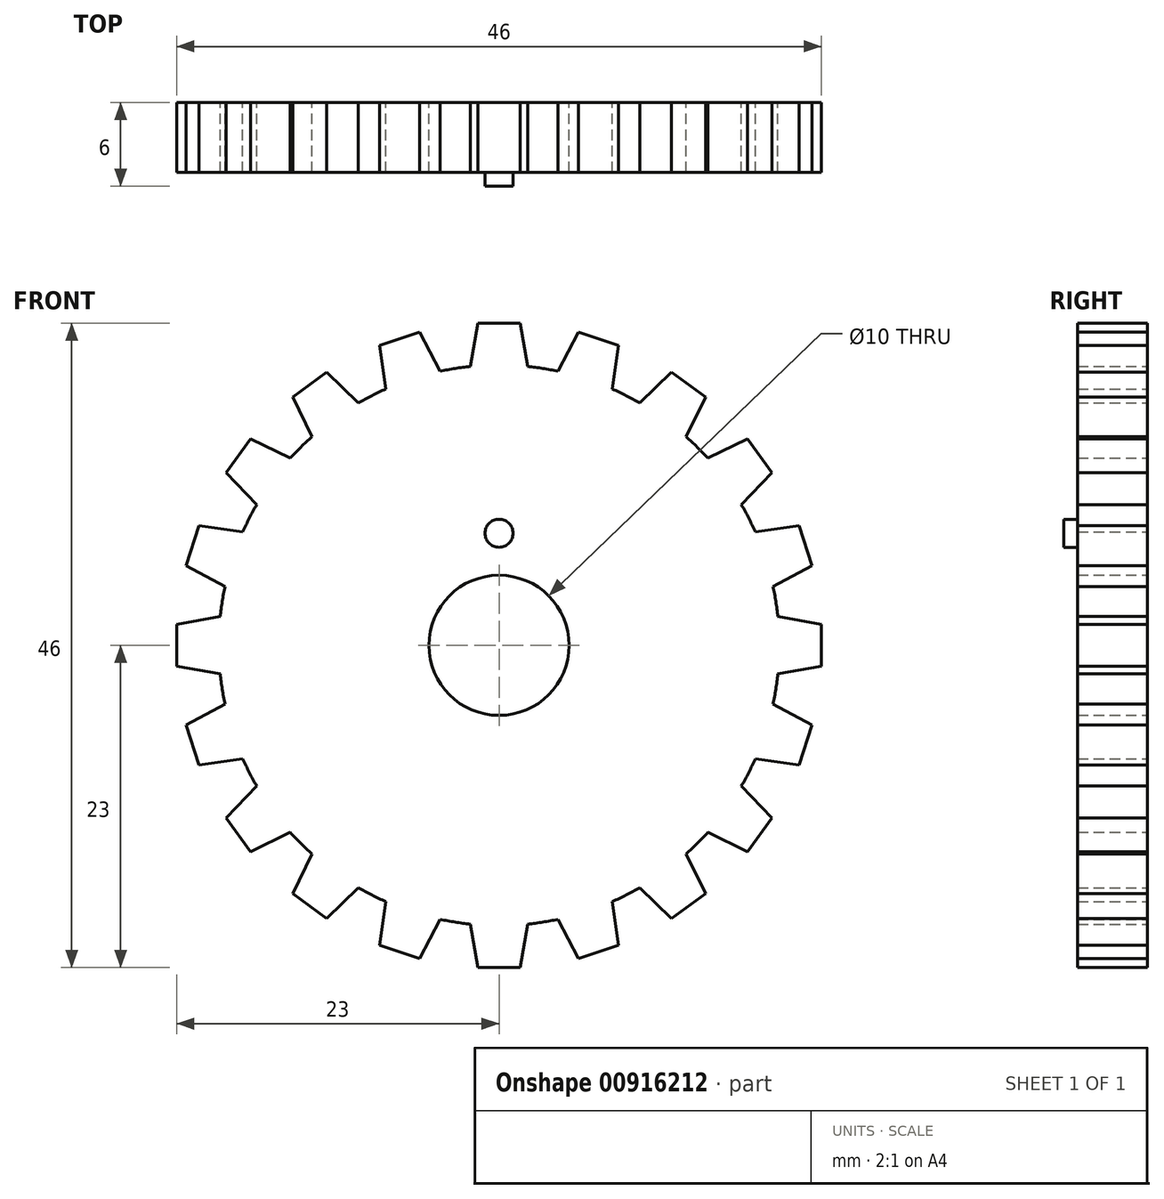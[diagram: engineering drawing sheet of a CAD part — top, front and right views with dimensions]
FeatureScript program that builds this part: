
annotation { "Feature Type Name" : "Feature", "Feature Type Description" : "" }
export const myFeature = defineFeature(function(context is Context, id is Id, definition is map)
    precondition{}
    {
        {
            var Q0;
            Q0=qCreatedBy(makeId("Front.planeOp"),FACE);
            var sketch = newSketch(context, id + "F0", { "sketchPlane" : qUnion([Q0])});
            skCircle(sketch, "E0", {"center": v(0, 0) * mm, "radius": 5 * mm});
            skCircle(sketch, "E1", {"center": v(0, 0) * mm, "radius": 20 * mm});
            skLineSegment(sketch, "E2", {"start": v(0, 23) * mm, "end": v(1.5, 23) * mm});
            skLineSegment(sketch, "E3", {"start": v(1.5, 23) * mm, "end": v(2.05, 19.9) * mm});
            skLineSegment(sketch, "E4.MirrorCS", {"start": v(0, 23) * mm, "end": v(-1.5, 23) * mm});
            skLineSegment(sketch, "E5.MirrorCS", {"start": v(-1.5, 23) * mm, "end": v(-2.05, 19.9) * mm});
            skLineSegment(sketch, "E6.1.0", {"start": v(-8.53, 21.41) * mm, "end": v(-8.1, 18.29) * mm});
            skLineSegment(sketch, "E6.1.1", {"start": v(-7.1, 21.87) * mm, "end": v(-8.53, 21.41) * mm});
            skLineSegment(sketch, "E6.1.2", {"start": v(-7.1, 21.87) * mm, "end": v(-5.68, 22.34) * mm});
            skLineSegment(sketch, "E6.1.3", {"start": v(-5.68, 22.34) * mm, "end": v(-4.2, 19.55) * mm});
            skLineSegment(sketch, "E6.2.0", {"start": v(-14.73, 17.73) * mm, "end": v(-13.35, 14.9) * mm});
            skLineSegment(sketch, "E6.2.1", {"start": v(-13.52, 18.6) * mm, "end": v(-14.73, 17.73) * mm});
            skLineSegment(sketch, "E6.2.2", {"start": v(-13.52, 18.6) * mm, "end": v(-12.3, 19.49) * mm});
            skLineSegment(sketch, "E6.2.3", {"start": v(-12.3, 19.49) * mm, "end": v(-10.04, 17.3) * mm});
            skLineSegment(sketch, "E7.2.3.0", {"start": v(-19.49, 12.3) * mm, "end": v(-17.3, 10.04) * mm});
            skLineSegment(sketch, "E7.3.3.0", {"start": v(-18.6, 13.52) * mm, "end": v(-19.49, 12.3) * mm});
            skLineSegment(sketch, "E7.6.3.0", {"start": v(-18.6, 13.52) * mm, "end": v(-17.73, 14.73) * mm});
            skLineSegment(sketch, "E7.9.3.0", {"start": v(-17.73, 14.73) * mm, "end": v(-14.9, 13.35) * mm});
            skLineSegment(sketch, "E7.2.4.0", {"start": v(-22.34, 5.68) * mm, "end": v(-19.55, 4.2) * mm});
            skLineSegment(sketch, "E7.3.4.0", {"start": v(-21.87, 7.1) * mm, "end": v(-22.34, 5.68) * mm});
            skLineSegment(sketch, "E7.6.4.0", {"start": v(-21.87, 7.1) * mm, "end": v(-21.41, 8.53) * mm});
            skLineSegment(sketch, "E7.9.4.0", {"start": v(-21.41, 8.53) * mm, "end": v(-18.29, 8.1) * mm});
            skLineSegment(sketch, "E7.2.5.0", {"start": v(-23, -1.5) * mm, "end": v(-19.9, -2.05) * mm});
            skLineSegment(sketch, "E7.3.5.0", {"start": v(-23, 0) * mm, "end": v(-23, -1.5) * mm});
            skLineSegment(sketch, "E7.6.5.0", {"start": v(-23, 0) * mm, "end": v(-23, 1.5) * mm});
            skLineSegment(sketch, "E7.9.5.0", {"start": v(-23, 1.5) * mm, "end": v(-19.9, 2.05) * mm});
            skLineSegment(sketch, "E7.2.6.0", {"start": v(-21.41, -8.53) * mm, "end": v(-18.29, -8.1) * mm});
            skLineSegment(sketch, "E7.3.6.0", {"start": v(-21.87, -7.1) * mm, "end": v(-21.41, -8.53) * mm});
            skLineSegment(sketch, "E7.6.6.0", {"start": v(-21.87, -7.1) * mm, "end": v(-22.34, -5.68) * mm});
            skLineSegment(sketch, "E7.9.6.0", {"start": v(-22.34, -5.68) * mm, "end": v(-19.55, -4.2) * mm});
            skLineSegment(sketch, "E7.2.7.0", {"start": v(-17.73, -14.73) * mm, "end": v(-14.9, -13.35) * mm});
            skLineSegment(sketch, "E7.3.7.0", {"start": v(-18.6, -13.52) * mm, "end": v(-17.73, -14.73) * mm});
            skLineSegment(sketch, "E7.6.7.0", {"start": v(-18.6, -13.52) * mm, "end": v(-19.49, -12.3) * mm});
            skLineSegment(sketch, "E7.9.7.0", {"start": v(-19.49, -12.3) * mm, "end": v(-17.3, -10.04) * mm});
            skLineSegment(sketch, "E7.2.8.0", {"start": v(-12.3, -19.49) * mm, "end": v(-10.04, -17.3) * mm});
            skLineSegment(sketch, "E7.3.8.0", {"start": v(-13.52, -18.6) * mm, "end": v(-12.3, -19.49) * mm});
            skLineSegment(sketch, "E7.6.8.0", {"start": v(-13.52, -18.6) * mm, "end": v(-14.73, -17.73) * mm});
            skLineSegment(sketch, "E7.9.8.0", {"start": v(-14.73, -17.73) * mm, "end": v(-13.35, -14.9) * mm});
            skLineSegment(sketch, "E7.2.9.0", {"start": v(-5.68, -22.34) * mm, "end": v(-4.2, -19.55) * mm});
            skLineSegment(sketch, "E7.3.9.0", {"start": v(-7.1, -21.87) * mm, "end": v(-5.68, -22.34) * mm});
            skLineSegment(sketch, "E7.6.9.0", {"start": v(-7.1, -21.87) * mm, "end": v(-8.53, -21.41) * mm});
            skLineSegment(sketch, "E7.9.9.0", {"start": v(-8.53, -21.41) * mm, "end": v(-8.1, -18.29) * mm});
            skLineSegment(sketch, "E8.2.10.0", {"start": v(1.5, -23) * mm, "end": v(2.05, -19.9) * mm});
            skLineSegment(sketch, "E8.3.10.0", {"start": v(0, -23) * mm, "end": v(1.5, -23) * mm});
            skLineSegment(sketch, "E8.6.10.0", {"start": v(0, -23) * mm, "end": v(-1.5, -23) * mm});
            skLineSegment(sketch, "E8.9.10.0", {"start": v(-1.5, -23) * mm, "end": v(-2.05, -19.9) * mm});
            skLineSegment(sketch, "E8.2.11.0", {"start": v(8.53, -21.41) * mm, "end": v(8.1, -18.29) * mm});
            skLineSegment(sketch, "E8.3.11.0", {"start": v(7.1, -21.87) * mm, "end": v(8.53, -21.41) * mm});
            skLineSegment(sketch, "E8.6.11.0", {"start": v(7.1, -21.87) * mm, "end": v(5.68, -22.34) * mm});
            skLineSegment(sketch, "E8.9.11.0", {"start": v(5.68, -22.34) * mm, "end": v(4.2, -19.55) * mm});
            skLineSegment(sketch, "E8.2.12.0", {"start": v(14.73, -17.73) * mm, "end": v(13.35, -14.9) * mm});
            skLineSegment(sketch, "E8.3.12.0", {"start": v(13.52, -18.6) * mm, "end": v(14.73, -17.73) * mm});
            skLineSegment(sketch, "E8.6.12.0", {"start": v(13.52, -18.6) * mm, "end": v(12.3, -19.49) * mm});
            skLineSegment(sketch, "E8.9.12.0", {"start": v(12.3, -19.49) * mm, "end": v(10.04, -17.3) * mm});
            skLineSegment(sketch, "E8.2.13.0", {"start": v(19.49, -12.3) * mm, "end": v(17.3, -10.04) * mm});
            skLineSegment(sketch, "E8.3.13.0", {"start": v(18.6, -13.52) * mm, "end": v(19.49, -12.3) * mm});
            skLineSegment(sketch, "E8.6.13.0", {"start": v(18.6, -13.52) * mm, "end": v(17.73, -14.73) * mm});
            skLineSegment(sketch, "E8.9.13.0", {"start": v(17.73, -14.73) * mm, "end": v(14.9, -13.35) * mm});
            skLineSegment(sketch, "E8.2.14.0", {"start": v(22.34, -5.68) * mm, "end": v(19.55, -4.2) * mm});
            skLineSegment(sketch, "E8.3.14.0", {"start": v(21.87, -7.1) * mm, "end": v(22.34, -5.68) * mm});
            skLineSegment(sketch, "E8.6.14.0", {"start": v(21.87, -7.1) * mm, "end": v(21.41, -8.53) * mm});
            skLineSegment(sketch, "E8.9.14.0", {"start": v(21.41, -8.53) * mm, "end": v(18.29, -8.1) * mm});
            skLineSegment(sketch, "E8.2.15.0", {"start": v(23, 1.5) * mm, "end": v(19.9, 2.05) * mm});
            skLineSegment(sketch, "E8.3.15.0", {"start": v(23, 0) * mm, "end": v(23, 1.5) * mm});
            skLineSegment(sketch, "E8.6.15.0", {"start": v(23, 0) * mm, "end": v(23, -1.5) * mm});
            skLineSegment(sketch, "E8.9.15.0", {"start": v(23, -1.5) * mm, "end": v(19.9, -2.05) * mm});
            skLineSegment(sketch, "E8.2.16.0", {"start": v(21.41, 8.53) * mm, "end": v(18.29, 8.1) * mm});
            skLineSegment(sketch, "E8.3.16.0", {"start": v(21.87, 7.1) * mm, "end": v(21.41, 8.53) * mm});
            skLineSegment(sketch, "E8.6.16.0", {"start": v(21.87, 7.1) * mm, "end": v(22.34, 5.68) * mm});
            skLineSegment(sketch, "E8.9.16.0", {"start": v(22.34, 5.68) * mm, "end": v(19.55, 4.2) * mm});
            skLineSegment(sketch, "E8.2.17.0", {"start": v(17.73, 14.73) * mm, "end": v(14.9, 13.35) * mm});
            skLineSegment(sketch, "E8.3.17.0", {"start": v(18.6, 13.52) * mm, "end": v(17.73, 14.73) * mm});
            skLineSegment(sketch, "E8.6.17.0", {"start": v(18.6, 13.52) * mm, "end": v(19.49, 12.3) * mm});
            skLineSegment(sketch, "E8.9.17.0", {"start": v(19.49, 12.3) * mm, "end": v(17.3, 10.04) * mm});
            skLineSegment(sketch, "E8.2.18.0", {"start": v(12.3, 19.49) * mm, "end": v(10.04, 17.3) * mm});
            skLineSegment(sketch, "E8.3.18.0", {"start": v(13.52, 18.6) * mm, "end": v(12.3, 19.49) * mm});
            skLineSegment(sketch, "E8.6.18.0", {"start": v(13.52, 18.6) * mm, "end": v(14.73, 17.73) * mm});
            skLineSegment(sketch, "E8.9.18.0", {"start": v(14.73, 17.73) * mm, "end": v(13.35, 14.9) * mm});
            skLineSegment(sketch, "E8.2.19.0", {"start": v(5.68, 22.34) * mm, "end": v(4.2, 19.55) * mm});
            skLineSegment(sketch, "E8.3.19.0", {"start": v(7.1, 21.87) * mm, "end": v(5.68, 22.34) * mm});
            skLineSegment(sketch, "E8.6.19.0", {"start": v(7.1, 21.87) * mm, "end": v(8.53, 21.41) * mm});
            skLineSegment(sketch, "E8.9.19.0", {"start": v(8.53, 21.41) * mm, "end": v(8.1, 18.29) * mm});
            skSolve(sketch);
        }
        {
            var Q0;
            Q0=qSketchRegion(id+"F0",true);
            extrude(context, id + "F1", {"entities" : qUnion([Q0]), "depth" : 5 * mm, "offsetDistance" : 25 * mm});
        }
        {
            var Q0;
            Q0=makeQuery(id+"F1.opExtrude","CAP_FACE",FACE,{"disambiguationData":[OSD([sQuery(id+"F0.wireOp",EDGE,"E0"),sQuery(id+"F0.wireOp",EDGE,"E1"),sQuery(id+"F0.wireOp",EDGE,"E2"),sQuery(id+"F0.wireOp",EDGE,"E3"),sQuery(id+"F0.wireOp",EDGE,"E4.MirrorCS"),sQuery(id+"F0.wireOp",EDGE,"E5.MirrorCS"),sQuery(id+"F0.wireOp",EDGE,"E6.1.0"),sQuery(id+"F0.wireOp",EDGE,"E6.1.1"),sQuery(id+"F0.wireOp",EDGE,"E6.1.2"),sQuery(id+"F0.wireOp",EDGE,"E6.1.3"),sQuery(id+"F0.wireOp",EDGE,"E6.2.0"),sQuery(id+"F0.wireOp",EDGE,"E6.2.1"),sQuery(id+"F0.wireOp",EDGE,"E6.2.2"),sQuery(id+"F0.wireOp",EDGE,"E6.2.3"),sQuery(id+"F0.wireOp",EDGE,"E7.2.3.0"),sQuery(id+"F0.wireOp",EDGE,"E7.3.3.0"),sQuery(id+"F0.wireOp",EDGE,"E7.6.3.0"),sQuery(id+"F0.wireOp",EDGE,"E7.9.3.0"),sQuery(id+"F0.wireOp",EDGE,"E7.2.4.0"),sQuery(id+"F0.wireOp",EDGE,"E7.3.4.0"),sQuery(id+"F0.wireOp",EDGE,"E7.6.4.0"),sQuery(id+"F0.wireOp",EDGE,"E7.9.4.0"),sQuery(id+"F0.wireOp",EDGE,"E7.2.5.0"),sQuery(id+"F0.wireOp",EDGE,"E7.3.5.0"),sQuery(id+"F0.wireOp",EDGE,"E7.6.5.0"),sQuery(id+"F0.wireOp",EDGE,"E7.9.5.0"),sQuery(id+"F0.wireOp",EDGE,"E7.2.6.0"),sQuery(id+"F0.wireOp",EDGE,"E7.3.6.0"),sQuery(id+"F0.wireOp",EDGE,"E7.6.6.0"),sQuery(id+"F0.wireOp",EDGE,"E7.9.6.0"),sQuery(id+"F0.wireOp",EDGE,"E7.2.7.0"),sQuery(id+"F0.wireOp",EDGE,"E7.3.7.0"),sQuery(id+"F0.wireOp",EDGE,"E7.6.7.0"),sQuery(id+"F0.wireOp",EDGE,"E7.9.7.0"),sQuery(id+"F0.wireOp",EDGE,"E7.2.8.0"),sQuery(id+"F0.wireOp",EDGE,"E7.3.8.0"),sQuery(id+"F0.wireOp",EDGE,"E7.6.8.0"),sQuery(id+"F0.wireOp",EDGE,"E7.9.8.0"),sQuery(id+"F0.wireOp",EDGE,"E7.2.9.0"),sQuery(id+"F0.wireOp",EDGE,"E7.3.9.0"),sQuery(id+"F0.wireOp",EDGE,"E7.6.9.0"),sQuery(id+"F0.wireOp",EDGE,"E7.9.9.0")])],"isStart":false});
            var sketch = newSketch(context, id + "F2", { "sketchPlane" : qUnion([Q0])});
            skCircle(sketch, "E9", {"center": v(0, 8) * mm, "radius": 1 * mm});
            skSolve(sketch);
        }
        {
            var Q0;
            Q0=qSketchRegion(id+"F2",true);
            extrude(context, id + "F3", {"entities" : qUnion([Q0]), "operationType" : NewBodyOperationType.ADD, "depth" : 1 * mm, "offsetDistance" : 25 * mm});
        }
    });
